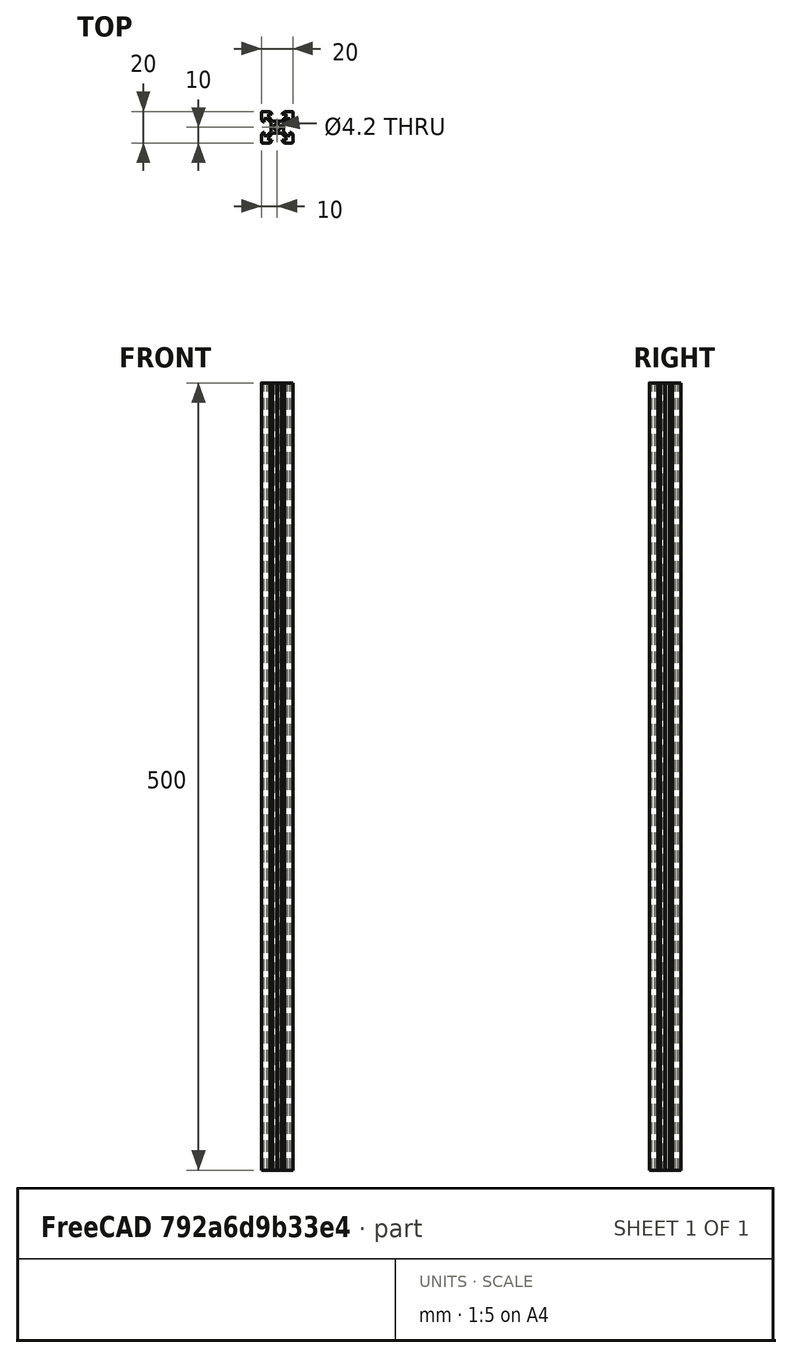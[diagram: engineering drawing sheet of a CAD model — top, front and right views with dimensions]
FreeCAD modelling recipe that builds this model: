
FCSTD DOCUMENT  (FreeCAD 0.19R)
Label: 2020-500
License: All rights reserved
LicenseURL: http://en.wikipedia.org/wiki/All_rights_reserved
objects: Sketcher::SketchObject×1, PartDesign::Pad×1, PartDesign::Body×1
note: 4 computed .brp shape members not serialized (recipe doc carries the construction recipe); baked Part::Feature solids carry a one-line shape summary decoded from their .brp

FEATURE [Sketcher::SketchObject] Sketch
  FullyConstrained = true
  MapMode = 5
  Support = -> [XY_Plane]
  sketch-geometry (65):
    g0: LineSegment StartX=-10 StartY=4.58 StartZ=0 EndX=-10 EndY=9.5 EndZ=0
    g1: LineSegment StartX=-9.5 StartY=10 StartZ=0 EndX=-4.58 EndY=10 EndZ=0
    g2: LineSegment StartX=-5.5 StartY=8.2 StartZ=0 EndX=-3.125 EndY=8.2 EndZ=0
    g3: LineSegment StartX=-8.2 StartY=5.5 StartZ=0 EndX=-8.2 EndY=3.125 EndZ=0
    g4: LineSegment StartX=-0.125 StartY=3.9 StartZ=0 EndX=-2.83934 EndY=3.9 EndZ=0
    g5: LineSegment StartX=-3.9 StartY=2.83934 StartZ=0 EndX=-3.9 EndY=0.125 EndZ=0
    g6: ArcOfCircle CenterX=0 CenterY=3.9 CenterZ=0 NormalX=0 NormalY=0 NormalZ=1 AngleXU=0 Radius=0.125 StartAngle=3.14159 EndAngle=6.28319
    g7: ArcOfCircle CenterX=-3.9 CenterY=0 CenterZ=0 NormalX=0 NormalY=0 NormalZ=1 AngleXU=0 Radius=0.125 StartAngle=4.71239 EndAngle=7.85398
    g8: ArcOfCircle CenterX=-9.5 CenterY=9.5 CenterZ=0 NormalX=0 NormalY=0 NormalZ=1 AngleXU=0 Radius=0.5 StartAngle=1.5708 EndAngle=3.14159
    g9: LineSegment StartX=-5.5 StartY=8.2 StartZ=0 EndX=-5.5 EndY=6.56066 EndZ=0
    g10: LineSegment StartX=-8.2 StartY=5.5 StartZ=0 EndX=-6.56066 EndY=5.5 EndZ=0
    g11: LineSegment StartX=-4.58 StartY=10 StartZ=0 EndX=-3.125 EndY=8.545 EndZ=0
    g12: LineSegment StartX=-3.125 StartY=8.545 StartZ=0 EndX=-3.125 EndY=8.2 EndZ=0
    g13: LineSegment StartX=-10 StartY=4.58 StartZ=0 EndX=-8.545 EndY=3.125 EndZ=0
    g14: LineSegment StartX=-8.545 StartY=3.125 StartZ=0 EndX=-8.2 EndY=3.125 EndZ=0
    g15: LineSegment StartX=-5.5 StartY=6.56066 StartZ=0 EndX=-2.83934 EndY=3.9 EndZ=0
    g16: LineSegment StartX=-6.56066 StartY=5.5 StartZ=0 EndX=-3.9 EndY=2.83934 EndZ=0
    g17: Circle CenterX=0 CenterY=0 CenterZ=0 NormalX=0 NormalY=0 NormalZ=1 AngleXU=0 Radius=2.1
    g18: LineSegment StartX=0.125 StartY=3.9 StartZ=0 EndX=2.83934 EndY=3.9 EndZ=0
    g19: LineSegment StartX=2.83934 StartY=3.9 StartZ=0 EndX=5.5 EndY=6.56066 EndZ=0
    g20: LineSegment StartX=5.5 StartY=6.56066 StartZ=0 EndX=5.5 EndY=8.2 EndZ=0
    g21: LineSegment StartX=3.125 StartY=8.2 StartZ=0 EndX=3.125 EndY=8.545 EndZ=0
    g22: LineSegment StartX=5.5 StartY=8.2 StartZ=0 EndX=3.125 EndY=8.2 EndZ=0
    g23: LineSegment StartX=4.58 StartY=10 StartZ=0 EndX=9.5 EndY=10 EndZ=0
    g24: ArcOfCircle CenterX=9.5 CenterY=9.5 CenterZ=0 NormalX=0 NormalY=0 NormalZ=1 AngleXU=0 Radius=0.5 StartAngle=1.9e-15 EndAngle=1.5708
    g25: LineSegment StartX=10 StartY=9.5 StartZ=0 EndX=10 EndY=4.58 EndZ=0
    g26: LineSegment StartX=10 StartY=4.58 StartZ=0 EndX=8.545 EndY=3.125 EndZ=0
    g27: LineSegment StartX=8.545 StartY=3.125 StartZ=0 EndX=8.2 EndY=3.125 EndZ=0
    g28: LineSegment StartX=8.2 StartY=3.125 StartZ=0 EndX=8.2 EndY=5.5 EndZ=0
    g29: LineSegment StartX=8.2 StartY=5.5 StartZ=0 EndX=6.56066 EndY=5.5 EndZ=0
    g30: LineSegment StartX=6.56066 StartY=5.5 StartZ=0 EndX=3.9 EndY=2.83934 EndZ=0
    g31: LineSegment StartX=3.9 StartY=2.83934 StartZ=0 EndX=3.9 EndY=0.125 EndZ=0
    g32: ArcOfCircle CenterX=3.9 CenterY=0 CenterZ=0 NormalX=0 NormalY=0 NormalZ=1 AngleXU=0 Radius=0.125 StartAngle=1.5708 EndAngle=4.71239
    g33: LineSegment StartX=3.9 StartY=-0.125 StartZ=0 EndX=3.9 EndY=-2.83934 EndZ=0
    g34: LineSegment StartX=3.9 StartY=-2.83934 StartZ=0 EndX=6.56066 EndY=-5.5 EndZ=0
    g35: LineSegment StartX=6.56066 StartY=-5.5 StartZ=0 EndX=8.2 EndY=-5.5 EndZ=0
    g36: LineSegment StartX=8.2 StartY=-5.5 StartZ=0 EndX=8.2 EndY=-3.125 EndZ=0
    g37: LineSegment StartX=8.2 StartY=-3.125 StartZ=0 EndX=8.545 EndY=-3.125 EndZ=0
    g38: LineSegment StartX=8.545 StartY=-3.125 StartZ=0 EndX=10 EndY=-4.58 EndZ=0
    g39: LineSegment StartX=10 StartY=-4.58 StartZ=0 EndX=10 EndY=-9.5 EndZ=0
    g40: ArcOfCircle CenterX=9.5 CenterY=-9.5 CenterZ=0 NormalX=0 NormalY=0 NormalZ=1 AngleXU=0 Radius=0.5 StartAngle=4.71239 EndAngle=6.28319
    g41: LineSegment StartX=9.5 StartY=-10 StartZ=0 EndX=4.58 EndY=-10 EndZ=0
    g42: LineSegment StartX=4.58 StartY=-10 StartZ=0 EndX=3.125 EndY=-8.545 EndZ=0
    g43: LineSegment StartX=2.83934 StartY=-3.9 StartZ=0 EndX=5.5 EndY=-6.56066 EndZ=0
    g44: LineSegment StartX=3.125 StartY=-8.545 StartZ=0 EndX=3.125 EndY=-8.2 EndZ=0
    g45: LineSegment StartX=3.125 StartY=-8.2 StartZ=0 EndX=5.5 EndY=-8.2 EndZ=0
    g46: LineSegment StartX=5.5 StartY=-8.2 StartZ=0 EndX=5.5 EndY=-6.56066 EndZ=0
    g47: ArcOfCircle CenterX=0 CenterY=-3.9 CenterZ=0 NormalX=0 NormalY=0 NormalZ=1 AngleXU=0 Radius=0.125 StartAngle=0 EndAngle=3.14159
    g48: LineSegment StartX=0.125 StartY=-3.9 StartZ=0 EndX=2.83934 EndY=-3.9 EndZ=0
    g49: LineSegment StartX=-0.125 StartY=-3.9 StartZ=0 EndX=-2.83934 EndY=-3.9 EndZ=0
    g50: LineSegment StartX=-3.9 StartY=-0.125 StartZ=0 EndX=-3.9 EndY=-2.83934 EndZ=0
    g51: LineSegment StartX=-3.9 StartY=-2.83934 StartZ=0 EndX=-6.56066 EndY=-5.5 EndZ=0
    g52: LineSegment StartX=-6.56066 StartY=-5.5 StartZ=0 EndX=-8.2 EndY=-5.5 EndZ=0
    g53: LineSegment StartX=-8.2 StartY=-5.5 StartZ=0 EndX=-8.2 EndY=-3.125 EndZ=0
    g54: LineSegment StartX=-8.2 StartY=-3.125 StartZ=0 EndX=-8.545 EndY=-3.125 EndZ=0
    g55: LineSegment StartX=-8.545 StartY=-3.125 StartZ=0 EndX=-10 EndY=-4.58 EndZ=0
    g56: LineSegment StartX=-10 StartY=-4.58 StartZ=0 EndX=-10 EndY=-9.5 EndZ=0
    g57: ArcOfCircle CenterX=-9.5 CenterY=-9.5 CenterZ=0 NormalX=0 NormalY=0 NormalZ=1 AngleXU=0 Radius=0.5 StartAngle=3.14159 EndAngle=4.71239
    g58: LineSegment StartX=-9.5 StartY=-10 StartZ=0 EndX=-4.58 EndY=-10 EndZ=0
    g59: LineSegment StartX=-4.58 StartY=-10 StartZ=0 EndX=-3.125 EndY=-8.545 EndZ=0
    g60: LineSegment StartX=-2.83934 StartY=-3.9 StartZ=0 EndX=-5.5 EndY=-6.56066 EndZ=0
    g61: LineSegment StartX=-5.5 StartY=-6.56066 StartZ=0 EndX=-5.5 EndY=-8.2 EndZ=0
    g62: LineSegment StartX=-5.5 StartY=-8.2 StartZ=0 EndX=-3.125 EndY=-8.2 EndZ=0
    g63: LineSegment StartX=-3.125 StartY=-8.545 StartZ=0 EndX=-3.125 EndY=-8.2 EndZ=0
    g64: LineSegment StartX=3.125 StartY=8.545 StartZ=0 EndX=4.58 EndY=10 EndZ=0
  constraints (194):
    c: Diameter(g17) = 4.2
    c: Radius(g32) = 0.125
    c: Coincident(g-1,g17)
    c: DistanceY(g57,g1) = 20
    c: DistanceX(g56,g39) = 20
    c: Radius(g57) = 0.5
    c: DistanceX(g56,g17) = 10
    c: DistanceY(g57,g17) = 10
    c: Distance(g5,g4) = 1.5
    c: DistanceY(g20,g23) = 1.8
    c: DistanceY(g18,g20) = 4.3
    c: DistanceX(g11,g21) = 6.25
    c: DistanceX(g1,g23) = 9.16
    c: DistanceX(g2,g20) = 11
    c: Coincident(g6,g18)
    c: Coincident(g6,g4)
    c: Coincident(g4,g15)
    c: Coincident(g18,g19)
    c: Coincident(g5,g16)
    c: Coincident(g16,g10)
    c: Coincident(g15,g9)
    c: Coincident(g12,g2)
    c: Coincident(g2,g9)
    c: Coincident(g12,g11)
    c: Coincident(g1,g11)
    c: Coincident(g23,g64)
    c: Coincident(g22,g21)
    c: Coincident(g64,g21)
    c: Coincident(g22,g20)
    c: Coincident(g19,g20)
    c: Coincident(g25,g26)
    c: Coincident(g27,g26)
    c: Coincident(g27,g28)
    c: Coincident(g28,g29)
    c: Coincident(g29,g30)
    c: Coincident(g0,g13)
    c: Coincident(g14,g13)
    c: Coincident(g14,g3)
    c: Coincident(g3,g10)
    c: Coincident(g5,g7)
    c: Coincident(g50,g7)
    c: Coincident(g51,g50)
    c: Coincident(g52,g51)
    c: Coincident(g52,g53)
    c: Coincident(g54,g53)
    c: Coincident(g55,g54)
    c: Coincident(g56,g55)
    c: Coincident(g58,g59)
    c: Coincident(g63,g59)
    c: Coincident(g62,g63)
    c: Coincident(g62,g61)
    c: Coincident(g60,g61)
    c: Coincident(g49,g60)
    c: Coincident(g47,g49)
    c: Coincident(g48,g47)
    c: Coincident(g48,g43)
    c: Coincident(g46,g43)
    c: Coincident(g45,g46)
    c: Coincident(g45,g44)
    c: Coincident(g42,g44)
    c: Coincident(g41,g42)
    c: Coincident(g39,g38)
    c: Coincident(g38,g37)
    c: Coincident(g37,g36)
    c: Coincident(g35,g36)
    c: Coincident(g34,g35)
    c: Coincident(g34,g33)
    c: Coincident(g31,g30)
    c: Coincident(g33,g32)
    c: Coincident(g32,g31)
    c: Vertical(g0)
    c: Horizontal(g1)
    c: Equal(g0,g1)
    c: Horizontal(g4)
    c: PointOnObject(g6,g-2)
    c: Horizontal(g18)
    c: Horizontal(g4,g6)
    c: Horizontal(g6,g6)
    c: Parallel(g13,g11)
    c: Horizontal(g14)
    c: Vertical(g12)
    c: Equal(g14,g12)
    c: Vertical(g3)
    c: Horizontal(g2)
    c: Equal(g3,g2)
    c: Equal(g10,g9)
    c: Horizontal(g10)
    c: Vertical(g9)
    c: Parallel(g16,g15)
    c: Equal(g13,g11)
    c: Tangent(g8,g0) = 1.5708
    c: PointOnObject(g7,g-1)
    c: Vertical(g5)
    c: Vertical(g50)
    c: Vertical(g7,g7)
    c: Vertical(g7,g5)
    c: Horizontal(g52)
    c: Vertical(g53)
    c: Horizontal(g54)
    c: Vertical(g56)
    c: Equal(g50,g5)
    c: Equal(g51,g16)
    c: Perpendicular(g16,g51)
    c: Equal(g52,g10)
    c: Equal(g53,g3)
    c: Equal(g54,g14)
    c: Equal(g55,g13)
    c: Perpendicular(g55,g13)
    c: Equal(g56,g0)
    c: Tangent(g57,g56) = -1.5708
    c: Tangent(g57,g58) = -1.5708
    c: Tangent(g8,g1) = 1.5708
    c: Equal(g57,g8)
    c: Horizontal(g58)
    c: Equal(g58,g56)
    c: Equal(g55,g59)
    c: Parallel(g55,g59)
    c: Vertical(g63)
    c: Equal(g63,g54)
    c: Horizontal(g62)
    c: Vertical(g61)
    c: Equal(g61,g52)
    c: Equal(g60,g51)
    c: Parallel(g60,g51)
    c: PointOnObject(g47,g-2)
    c: Horizontal(g47,g47)
    c: Horizontal(g47,g47)
    c: Horizontal(g49)
    c: Equal(g49,g50)
    c: Horizontal(g48)
    c: Vertical(g46)
    c: Perpendicular(g60,g43)
    c: Equal(g43,g60)
    c: Equal(g46,g61)
    c: Horizontal(g45)
    c: Equal(g45,g62)
    c: Vertical(g44)
    c: Equal(g44,g63)
    c: Perpendicular(g42,g59)
    c: Equal(g42,g59)
    c: Horizontal(g41)
    c: Equal(g58,g41)
    c: Tangent(g40,g41) = 1.5708
    c: Tangent(g40,g39) = 1.5708
    c: Equal(g57,g40)
    c: Vertical(g39)
    c: Equal(g41,g39)
    c: Parallel(g42,g38)
    c: Equal(g42,g38)
    c: Horizontal(g37)
    c: Equal(g44,g37)
    c: Vertical(g36)
    c: Equal(g45,g36)
    c: Horizontal(g35)
    c: Equal(g35,g46)
    c: Parallel(g43,g34)
    c: Equal(g43,g34)
    c: PointOnObject(g32,g-1)
    c: Vertical(g33)
    c: Vertical(g32,g31)
    c: Vertical(g31,g32)
    c: Equal(g48,g33)
    c: Equal(g47,g7)
    c: Equal(g7,g6)
    c: Vertical(g31)
    c: Equal(g33,g31)
    c: Equal(g4,g5)
    c: Equal(g4,g18)
    c: Parallel(g30,g19)
    c: Equal(g30,g19)
    c: Horizontal(g29)
    c: Vertical(g20)
    c: Equal(g35,g29)
    c: Equal(g29,g20)
    c: Horizontal(g22)
    c: Equal(g22,g2)
    c: Vertical(g21)
    c: Equal(g11,g64)
    c: Horizontal(g23)
    c: Equal(g1,g23)
    c: Vertical(g28)
    c: Equal(g28,g36)
    c: Horizontal(g27)
    c: Equal(g27,g37)
    c: Perpendicular(g38,g26)
    c: Equal(g38,g26)
    c: Vertical(g25)
    c: Equal(g39,g25)
    c: Tangent(g24,g23) = 1.5708
    c: Tangent(g24,g25) = 1.5708
    c: Vertical(g25,g38)
    c: Horizontal(g2,g21)
    c: Vertical(g10,g51)
    c: Angle(g64,g11) = 1.5708
FEATURE [PartDesign::Pad] Pad
  Direction = (1,1,1)
  Length = 500
  Length2 = 100
  Profile = -> Sketch
  Type = 0
FEATURE [PartDesign::Body] Body  label="2020-500"
  Group = -> [Sketch,Pad]
  Origin = -> Origin
  Tip = -> Pad
